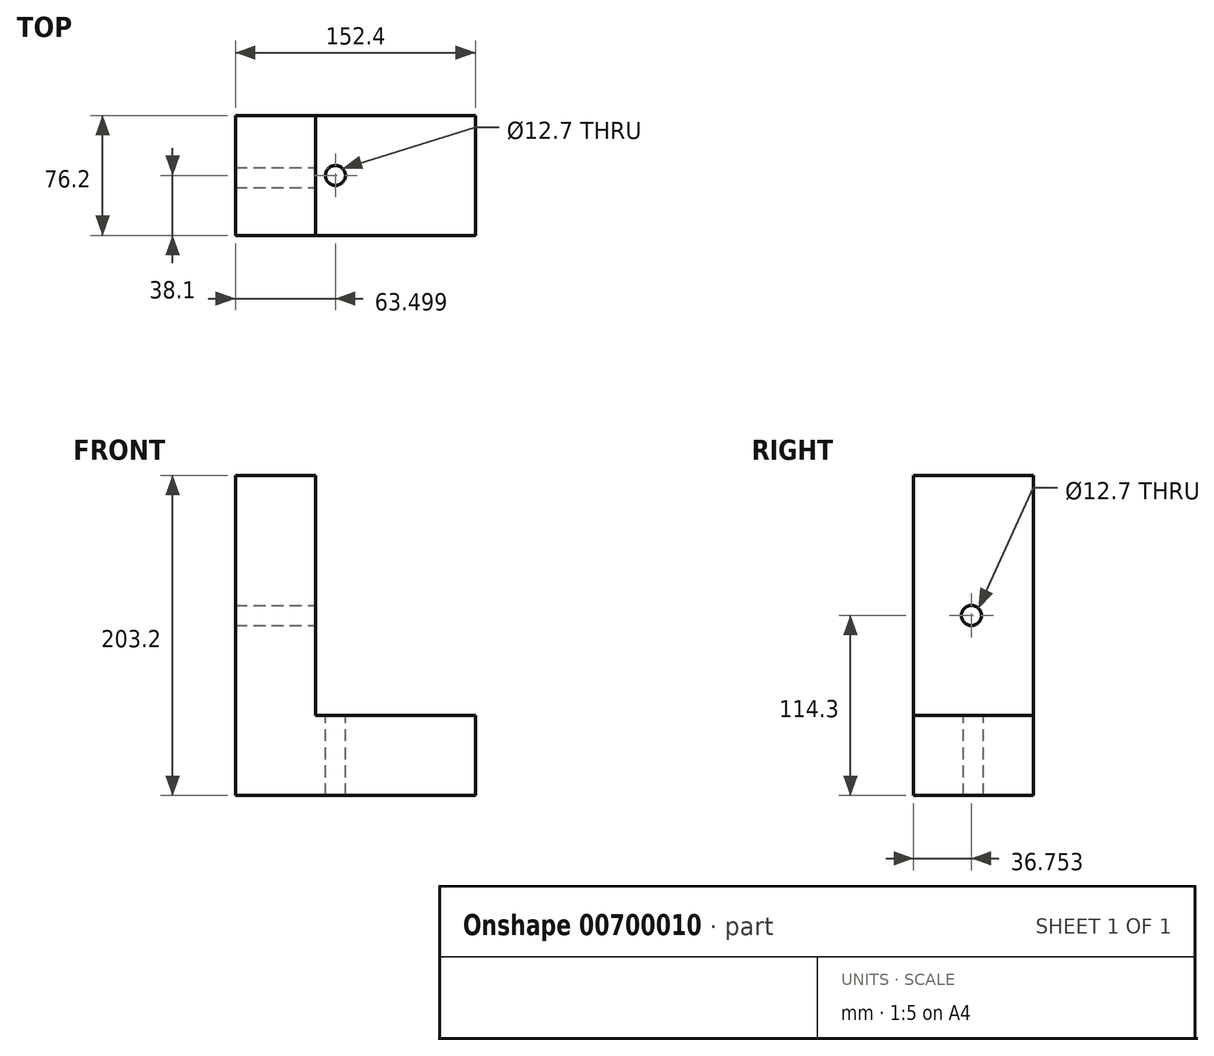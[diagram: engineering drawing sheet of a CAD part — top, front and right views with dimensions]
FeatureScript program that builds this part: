
annotation { "Feature Type Name" : "Feature", "Feature Type Description" : "" }
export const myFeature = defineFeature(function(context is Context, id is Id, definition is map)
    precondition{}
    {
        {
            var Q0;
            Q0=qCreatedBy(makeId("Front.planeOp"),FACE);
            var sketch = newSketch(context, id + "F0", { "sketchPlane" : qUnion([Q0])});
            skLineSegment(sketch, "E0", {"start": v(-73.75, 152.4) * mm, "end": v(-73.75, -50.8) * mm});
            skLineSegment(sketch, "E1", {"start": v(-73.75, -50.8) * mm, "end": v(78.65, -50.8) * mm});
            skLineSegment(sketch, "E2", {"start": v(78.65, -50.8) * mm, "end": v(78.65, 0) * mm});
            skLineSegment(sketch, "E3", {"start": v(78.65, 0) * mm, "end": v(-22.95, 0) * mm});
            skLineSegment(sketch, "E4", {"start": v(-22.95, 0) * mm, "end": v(-22.95, 152.4) * mm});
            skLineSegment(sketch, "E5", {"start": v(-22.95, 152.4) * mm, "end": v(-73.75, 152.4) * mm});
            skSolve(sketch);
        }
        {
            var Q0;
            Q0 = qSketchRegion(id + "F0", true);
            extrude(context, id + "F1", {"entities" : qUnion([Q0]), "depth" : 76.2 * mm, "offsetDistance" : 25.4 * mm});
        }
        {
            var Q0;
            Q0=makeQuery(id+"F1.opExtrude","SWEPT_FACE",FACE,{"disambiguationData":[OSD([sQuery(id+"F0.wireOp",EDGE,"E4")])]});
            var sketch = newSketch(context, id + "F2", { "sketchPlane" : qUnion([Q0])});
            skPoint(sketch, "E6", {"position": v(-39.45, 63.5) * mm});
            skSolve(sketch);
        }
        {
            var Q0;
            Q0=makeQuery(id+"F1.opExtrude","SWEPT_FACE",FACE,{"disambiguationData":[OSD([sQuery(id+"F0.wireOp",EDGE,"E3")])]});
            var sketch = newSketch(context, id + "F3", { "sketchPlane" : qUnion([Q0])});
            skPoint(sketch, "E7", {"position": v(-10.25, -38.1) * mm});
            skPoint(sketch, "E7.positionSnap0", {"position": v(-22.95, -38.1) * mm});
            skSolve(sketch);
        }
        {
            var Q0;
            Q0=sQuery(id+"F2.wireOp",VERTEX,"E6");
            var Q1;
            Q1=makeQuery(id+"F1.opExtrude","SWEPT_BODY",BODY,{"disambiguationData":[OSD([sQuery(id+"F0.wireOp",EDGE,"E0"),sQuery(id+"F0.wireOp",EDGE,"E1"),sQuery(id+"F0.wireOp",EDGE,"E2"),sQuery(id+"F0.wireOp",EDGE,"E3"),sQuery(id+"F0.wireOp",EDGE,"E4"),sQuery(id+"F0.wireOp",EDGE,"E5")])]});
            hole(context, id + "F4", {"style" : HoleStyle.SIMPLE, "endStyle" : HoleEndStyle.THROUGH, "holeDiameter" : 12.7 * mm, "majorDiameter" : 6.35 * mm, "isTappedThrough" : true, "tappedDepth" : 12.7 * mm, "tapClearance" : 3, "locations" : qUnion([Q0]), "scope" : qUnion([Q1])});
        }
        {
            var Q0;
            Q0=sQuery(id+"F3.wireOp",VERTEX,"E7");
            var Q1;
            Q1=makeQuery(id+"F1.opExtrude","SWEPT_BODY",BODY,{"disambiguationData":[OSD([sQuery(id+"F0.wireOp",EDGE,"E0"),sQuery(id+"F0.wireOp",EDGE,"E1"),sQuery(id+"F0.wireOp",EDGE,"E2"),sQuery(id+"F0.wireOp",EDGE,"E3"),sQuery(id+"F0.wireOp",EDGE,"E4"),sQuery(id+"F0.wireOp",EDGE,"E5")])]});
            hole(context, id + "F5", {"style" : HoleStyle.SIMPLE, "endStyle" : HoleEndStyle.THROUGH, "holeDiameter" : 12.7 * mm, "majorDiameter" : 6.35 * mm, "isTappedThrough" : true, "tappedDepth" : 12.7 * mm, "tapClearance" : 3, "locations" : qUnion([Q0]), "scope" : qUnion([Q1])});
        }
    });
